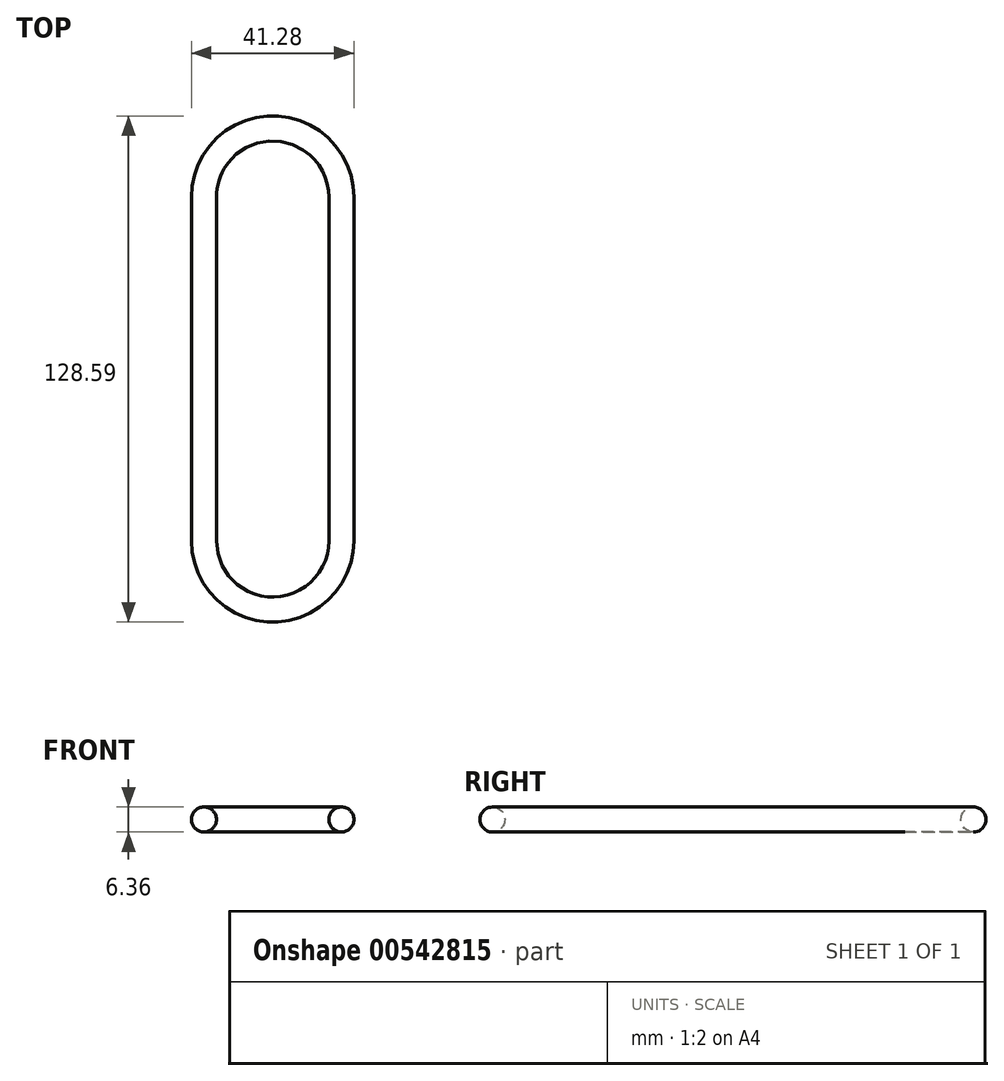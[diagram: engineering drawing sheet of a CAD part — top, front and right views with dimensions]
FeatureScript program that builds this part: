
annotation { "Feature Type Name" : "Feature", "Feature Type Description" : "" }
export const myFeature = defineFeature(function(context is Context, id is Id, definition is map)
    precondition{}
    {
        {
            var Q0;
            Q0=qCreatedBy(makeId("Top.planeOp"),FACE);
            var sketch = newSketch(context, id + "F0", { "sketchPlane" : qUnion([Q0])});
            skArc(sketch, "E0", {"start": v(-17.46, -87.31) * mm, "mid": v(0, -104.78) * mm, "end": v(17.46, -87.31) * mm});
            skArc(sketch, "E1", {"start": v(17.46, 0) * mm, "mid": v(0, 17.46) * mm, "end": v(-17.46, 0) * mm});
            skLineSegment(sketch, "E2", {"start": v(-17.46, 0) * mm, "end": v(-17.46, -87.31) * mm});
            skLineSegment(sketch, "E3", {"start": v(17.46, 0) * mm, "end": v(17.46, -87.31) * mm});
            skSolve(sketch);
        }
        {
            var Q0;
            Q0=qCreatedBy(makeId("Front.planeOp"),FACE);
            var sketch = newSketch(context, id + "F1", { "sketchPlane" : qUnion([Q0])});
            skCircle(sketch, "E4", {"center": v(-17.46, 0) * mm, "radius": 3.18 * mm});
            skSolve(sketch);
        }
        {
            var Q0;
            Q0=makeQuery(id+"F1.imprint","IMPRINT",FACE,{"disambiguationData":[TD([[makeQuery(id+"F1.imprint","IMPRINT",EDGE,{"derivedFrom":sQuery(id+"F1.wireOp",EDGE,"E4")}),1.0]])]});
            var Q1;
            Q1=sQuery(id+"F0.wireOp",EDGE,"E2");
            var Q2;
            Q2=sQuery(id+"F0.wireOp",EDGE,"E0");
            var Q3;
            Q3=sQuery(id+"F0.wireOp",EDGE,"E3");
            var Q4;
            Q4=sQuery(id+"F0.wireOp",EDGE,"E1");
            sweep(context, id + "F2", {"profiles" : qUnion([Q0]), "path" : qUnion([Q1, Q2, Q3, Q4])});
        }
    });
